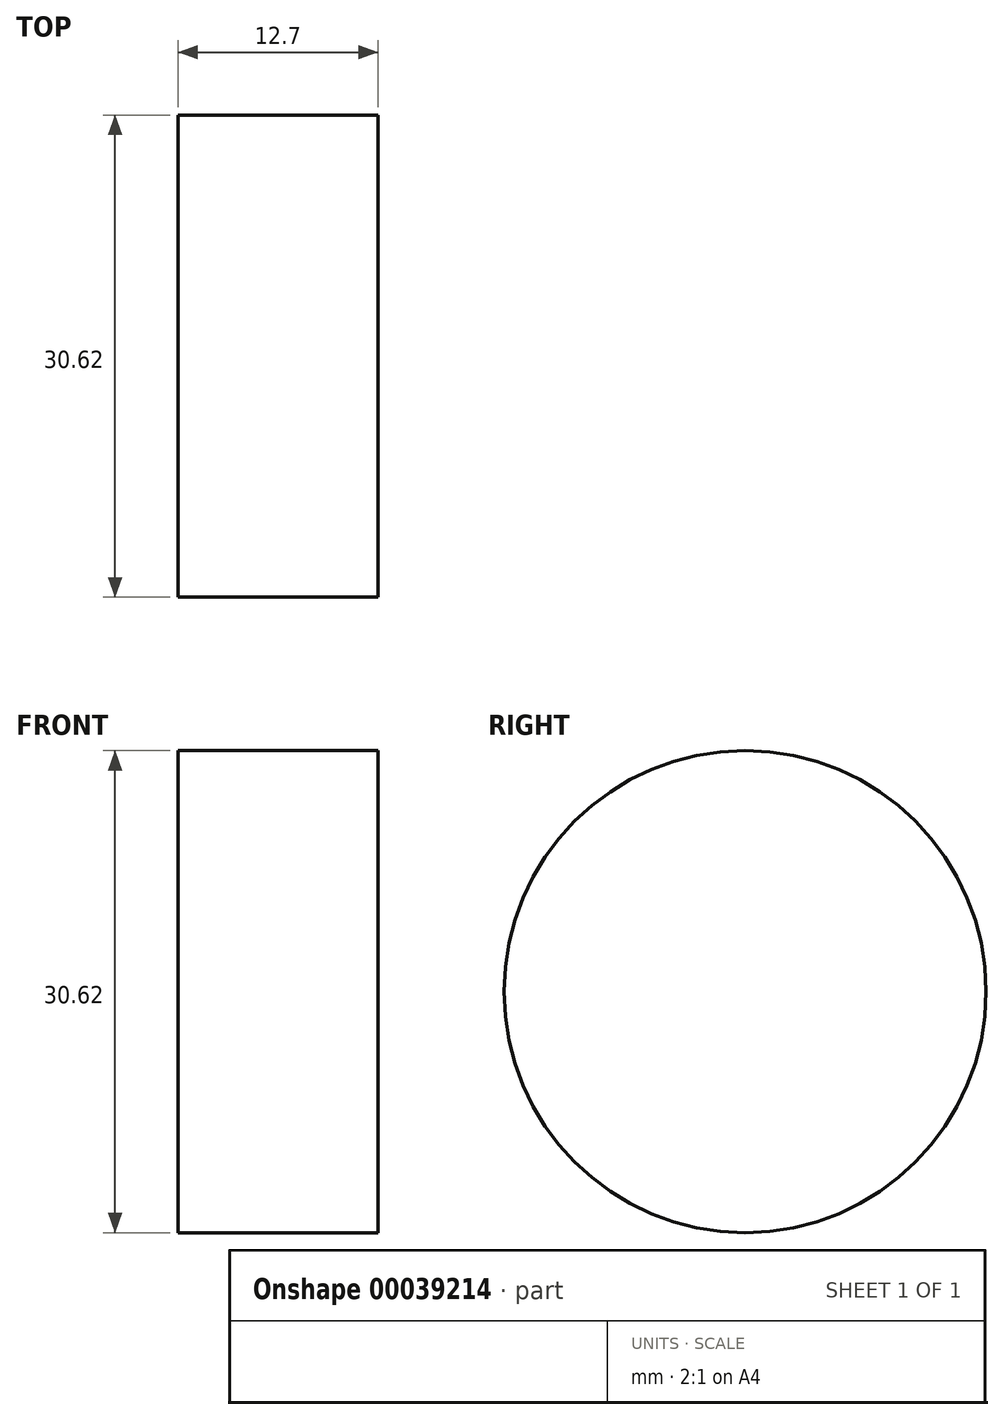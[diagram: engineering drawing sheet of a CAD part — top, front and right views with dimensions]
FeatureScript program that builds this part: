
annotation { "Feature Type Name" : "Feature", "Feature Type Description" : "" }
export const myFeature = defineFeature(function(context is Context, id is Id, definition is map)
    precondition{}
    {
        {
            var Q0;
            Q0=qCreatedBy(makeId("Right.planeOp"),FACE);
            var sketch = newSketch(context, id + "F0", { "sketchPlane" : qUnion([Q0])});
            skCircle(sketch, "E0", {"center": v(0, 0) * mm, "radius": 15.3 * mm});
            skSolve(sketch);
        }
        {
            var Q0;
            Q0=makeQuery(id+"F0.imprint","IMPRINT",FACE,{"disambiguationData":[TD([[makeQuery(id+"F0.imprint","IMPRINT",EDGE,{"derivedFrom":sQuery(id+"F0.wireOp",EDGE,"E0")}),1.0]])]});
            extrude(context, id + "F1", {"entities" : qUnion([Q0]), "depth" : 12.7 * mm});
        }
    });
